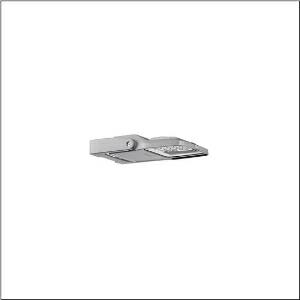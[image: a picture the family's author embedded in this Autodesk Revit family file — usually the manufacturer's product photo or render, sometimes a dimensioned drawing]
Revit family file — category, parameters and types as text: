
# Revit family: floodlight_fl_21_iq_micro___pl61_5xa7762a4c2a_69cd
name_source: partatom
category: Lighting Fixtures
units: mm (PartAtom-declared; Revit-internal decimal feet)

## family parameters
Cut with Voids When Loaded = No
Host = Face
Light Source = No
Part Type = Normal
Room Calculation Point = No
Round Connector Dimension = Use Diameter
Shared = No

## types (1)
- --- (1 x LED, 3030 lm, 23.1 W, 4000K)
    Apparent Load = 23 VA
    CIE Flux Codes = 33 65 98 100 100
    Color Rendering = 70
    Color Temperature = 4000K
    Default Elevation = 1800 mm
    Description = Floodlight FL 21 iQ micro, floodlight, primary light control with lens, of PMMA, primary optical cover: protective disc, of toughened safety glass, transparent, light distribution: PL61, light emission: direct distribution, installation type: surface-mounted, lamps: LED, High Power LED, rated values: 3.030lm | 23,1W | 131,2lm/W (begin service life); end service life: 3.030lm | 23,8W; at 50% lumin. flux: 1.515lm | 11W | 137,7lm/W, colour temperature: 4000K, colour rendering: CRI > 70, light colour: 740, light setting 1 begin service life: 100% | 3.030lm | 23,1W | 131,2lm/W | 4.000K, light setting 1 end service life: 23,8W, further light settings possible, control: Auto-Match, Temp-Guard, Night-Set, Smart-Wire, Desk-Remote (wireless, voltage-free reading and setting of iQ features in the workshop via application-optimized NFC function/RFID function), optimised constant luminous flux control (CLO 2.0), Street-Remote, pre-setting: linear dimming characteristic, with terminal, 6-pole, mains connection: 220..240V, AC, 50/60Hz, luminaire housing, of diecast aluminium, powder-coated, SITECO metallic grey (DB 702S), corrosivity category C5 mid according to DIN EN ISO 12944suitable for swimming poolschlorine-resistant, sealing non-destructively replaceable, design bracket, of diecast aluminium, powder-coated, SITECO metallic grey (DB 702S), protection rating (complete): IP66, insulation class (complete): insulation class II (safety insulation), certification: CE, ENEC, VDE, protection symbol: D, impact resistance: IK07, permissible operating ambient temperature: -40..+40°C, permissible operating ambient temperature for outdoor applications: -40..+50°C, standard: DIN EN 12944, LABS conformity tested according to VDMA 24364:2018-05, packaging unit: 1 piece

Light Distribution: PL61
    Height = 65 mm
    Lamp = 1 x LED
    Lamp Light Flux = 3030 lm
    Lamp Power = 23.1 W
    Lamp count = 1
    Length = 312 mm
    Luminous efficacy = 131 lm/W
    Manufacturer = Siteco
    ModVariant = No
    Model = 5XA7762A4C2A
    Mounting Place = Wall
    Mounting Type = Surface mounted
    Number of Poles = 1
    OnlyDefault = Yes
    Power Factor = 1
    Product Name = Floodlight FL 21 iQ micro | PL61
    Product group = floodlight | wall mounted
    ProductGroupID = 2002
    Protection Class = Protection class II
    Protection Degree = IP 66
    RLX_Detail_Level = 1
    RLX_Emergency_Light_Flux = 0 lm
    RLX_Emergency_Type = 0
    RLX_Emergency_Type_DB = No
    RlxData = <blob elided: 97701 chars, md5=70882168>
    Socket = socket
    Standby Power = 0 W
    System Light Flux = 3030 lm
    System Power = 23 W
    Type Comments = factory setting: luminous flux: 100 % | dim-lin: 254 | 455 mA
    Type Image = l_1006878.jpg
    URL = http://relux.com
    VarID = @adj_191761
    Voltage = 0 V
    Weight = 0.00 kg
    Width = 230 mm

## geometry (parser evidence)
native form markers: Blend x4, Sweep x12
no freeform markers — native parametric forms only
